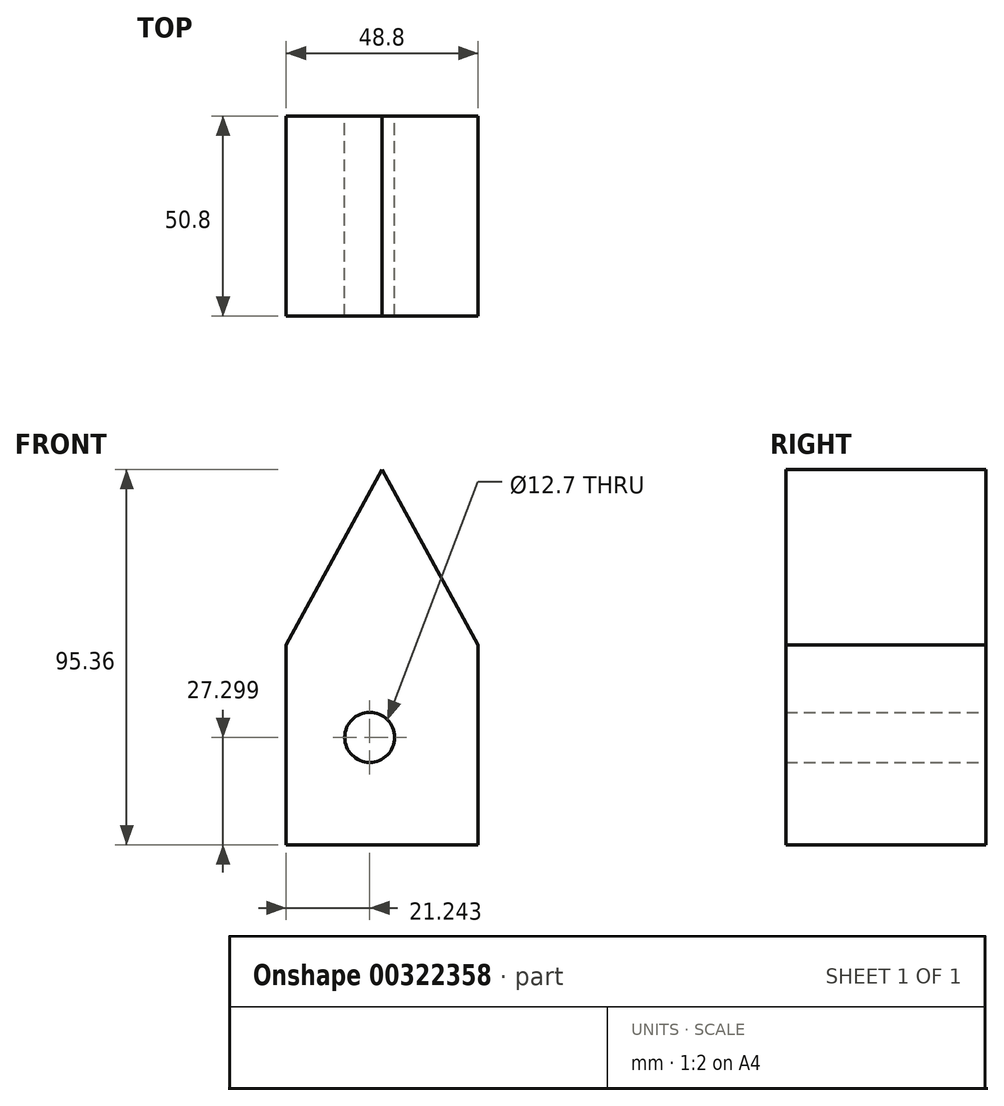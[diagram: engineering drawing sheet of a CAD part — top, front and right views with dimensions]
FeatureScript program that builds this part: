
annotation { "Feature Type Name" : "Feature", "Feature Type Description" : "" }
export const myFeature = defineFeature(function(context is Context, id is Id, definition is map)
    precondition{}
    {
        {
            var Q0;
            Q0=qCreatedBy(makeId("Front.planeOp"),FACE);
            var sketch = newSketch(context, id + "F0", { "sketchPlane" : qUnion([Q0])});
            skLineSegment(sketch, "E0.bottom", {"start": v(24.4, -32.52) * mm, "end": v(-24.4, -32.52) * mm});
            skLineSegment(sketch, "E0.left", {"start": v(24.4, -32.52) * mm, "end": v(24.4, 18.28) * mm});
            skLineSegment(sketch, "E0.right", {"start": v(-24.4, -32.52) * mm, "end": v(-24.4, 18.28) * mm});
            skLineSegment(sketch, "E1", {"start": v(-24.4, 18.28) * mm, "end": v(0, 62.84) * mm});
            skLineSegment(sketch, "E2", {"start": v(24.4, 18.28) * mm, "end": v(0, 62.84) * mm});
            skCircle(sketch, "E3", {"center": v(-3.16, -5.22) * mm, "radius": 6.35 * mm});
            skSolve(sketch);
        }
        {
            var Q0;
            Q0=makeQuery(id+"F0.imprint","IMPRINT",FACE,{"disambiguationData":[TD([[makeQuery(id+"F0.imprint","IMPRINT",EDGE,{"derivedFrom":sQuery(id+"F0.wireOp",EDGE,"E0.bottom")}),-1.0]])]});
            extrude(context, id + "F1", {"entities" : qUnion([Q0]), "depth" : 50.8 * mm});
        }
    });
